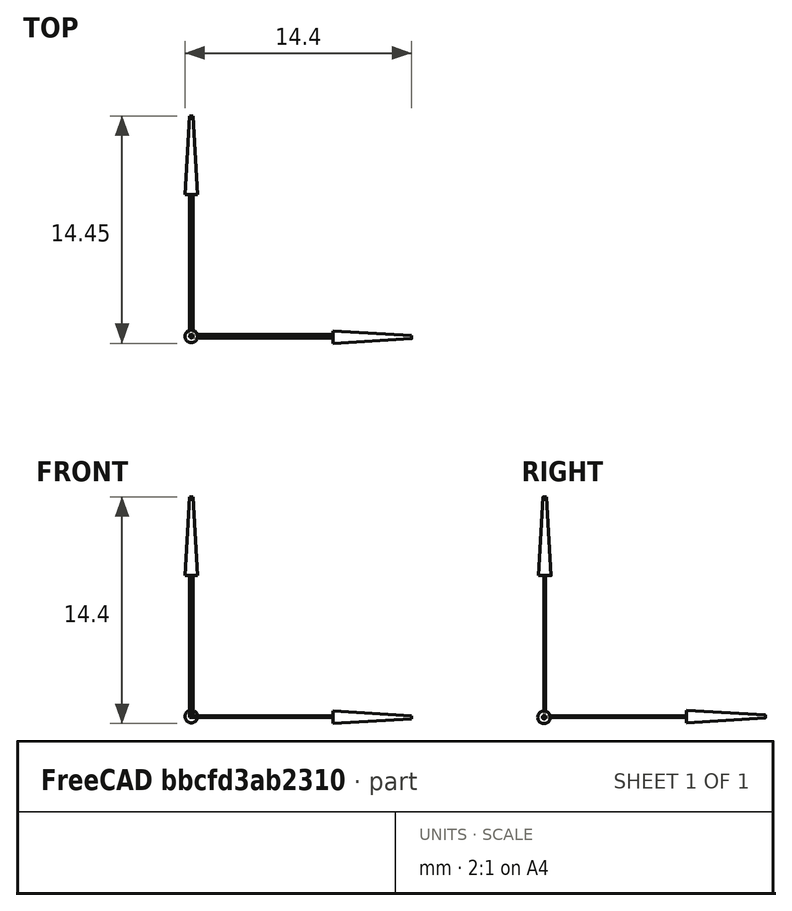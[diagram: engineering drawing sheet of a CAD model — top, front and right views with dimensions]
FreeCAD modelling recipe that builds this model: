
FCSTD DOCUMENT  (FreeCAD 0.16R6458 (Git))
Label: TSM-104-02-X-DH
License: All rights reserved
LicenseURL: http://en.wikipedia.org/wiki/All_rights_reserved
objects: Part::Feature×3, Sketcher::SketchObject×2, App::DocumentObjectGroup×1
note: 5 computed .brp shape members not serialized (recipe doc carries the construction recipe); baked Part::Feature solids carry a one-line shape summary decoded from their .brp

FEATURE [Part::Feature] FusionAxisZ1  label="Z"
  shape: bbox 0.8 x 0.8 x 14 mm, 8 faces (baked)
FEATURE [Part::Feature] FusionAxisY1  label="Y"
  Placement = pos=(0,0,0.05) rot=(-1,0,0;1.5708rad)
  shape: bbox 0.8 x 14 x 0.8 mm, 8 faces (baked)
FEATURE [Part::Feature] FusionAxisX1  label="X"
  Placement = pos=(0,-0.05,0) rot=(0,1,0;1.5708rad)
  shape: bbox 14 x 0.8 x 0.8 mm, 8 faces (baked)
FEATURE [App::DocumentObjectGroup] axis
  Group = -> [FusionAxisZ1,FusionAxisY1,FusionAxisX1]
FEATURE [Sketcher::SketchObject] Sketch001  label="Silcsreen_Helper"
  expr: Constraints[10] = 4 * 2.54mm
  sketch-geometry (4):
    g0: LineSegment StartX=0 StartY=-5.08 StartZ=0 EndX=2.54 EndY=-5.08 EndZ=0
    g1: LineSegment StartX=2.54 StartY=-5.08 StartZ=0 EndX=2.54 EndY=5.08 EndZ=0
    g2: LineSegment StartX=2.54 StartY=5.08 StartZ=0 EndX=0 EndY=5.08 EndZ=0
    g3: LineSegment StartX=0 StartY=5.08 StartZ=0 EndX=0 EndY=-5.08 EndZ=0
  constraints (11):
    c: Coincident(g0,g1)
    c: Coincident(g1,g2)
    c: Coincident(g2,g3)
    c: Coincident(g3,g0)
    c: Horizontal(g0)
    c: Horizontal(g2)
    c: Vertical(g1)
    c: Vertical(g3)
    c: Symmetric(g3,g3,g-1)
    c: DistanceX(g0) = 2.54
    c: DistanceY(g1) = 10.16
FEATURE [Sketcher::SketchObject] Sketch002  label="Footprint_Helper"
  expr: Constraints[133] = 1.19 / 2
  expr: Constraints[129] = (4 - 2) * 2.54mm
  expr: Constraints[10] = 4 * 2.54mm
  sketch-geometry (59):
    g0: LineSegment StartX=0 StartY=-5.08 StartZ=0 EndX=2.54 EndY=-5.08 EndZ=0
    g1: LineSegment StartX=2.54 StartY=-5.08 StartZ=0 EndX=2.54 EndY=5.08 EndZ=0
    g2: LineSegment StartX=2.54 StartY=5.08 StartZ=0 EndX=0 EndY=5.08 EndZ=0
    g3: LineSegment StartX=0 StartY=5.08 StartZ=0 EndX=0 EndY=-5.08 EndZ=0
    g4: LineSegment StartX=4.176 StartY=4.445 StartZ=0 EndX=7.356 EndY=4.445 EndZ=0
    g5: LineSegment StartX=7.356 StartY=4.445 StartZ=0 EndX=7.356 EndY=3.175 EndZ=0
    g6: LineSegment StartX=7.356 StartY=3.175 StartZ=0 EndX=4.176 EndY=3.175 EndZ=0
    g7: LineSegment StartX=4.176 StartY=3.175 StartZ=0 EndX=4.176 EndY=4.445 EndZ=0
    g8: LineSegment StartX=7.986 StartY=4.445 StartZ=0 EndX=11.166 EndY=4.445 EndZ=0
    g9: LineSegment StartX=11.166 StartY=4.445 StartZ=0 EndX=11.166 EndY=3.175 EndZ=0
    g10: LineSegment StartX=11.166 StartY=3.175 StartZ=0 EndX=7.986 EndY=3.175 EndZ=0
    g11: LineSegment StartX=7.986 StartY=3.175 StartZ=0 EndX=7.986 EndY=4.445 EndZ=0
    g12: LineSegment StartX=4.176 StartY=1.905 StartZ=0 EndX=7.356 EndY=1.905 EndZ=0
    g13: LineSegment StartX=7.356 StartY=1.905 StartZ=0 EndX=7.356 EndY=0.635 EndZ=0
    g14: LineSegment StartX=7.356 StartY=0.635 StartZ=0 EndX=4.176 EndY=0.635 EndZ=0
    g15: LineSegment StartX=4.176 StartY=0.635 StartZ=0 EndX=4.176 EndY=1.905 EndZ=0
    g16: LineSegment StartX=7.986 StartY=1.905 StartZ=0 EndX=11.166 EndY=1.905 EndZ=0
    g17: LineSegment StartX=11.166 StartY=1.905 StartZ=0 EndX=11.166 EndY=0.635 EndZ=0
    g18: LineSegment StartX=11.166 StartY=0.635 StartZ=0 EndX=7.986 EndY=0.635 EndZ=0
    g19: LineSegment StartX=7.986 StartY=0.635 StartZ=0 EndX=7.986 EndY=1.905 EndZ=0
    g20: LineSegment StartX=4.176 StartY=-0.635 StartZ=0 EndX=7.356 EndY=-0.635 EndZ=0
    g21: LineSegment StartX=7.356 StartY=-0.635 StartZ=0 EndX=7.356 EndY=-1.905 EndZ=0
    g22: LineSegment StartX=7.356 StartY=-1.905 StartZ=0 EndX=4.176 EndY=-1.905 EndZ=0
    g23: LineSegment StartX=4.176 StartY=-1.905 StartZ=0 EndX=4.176 EndY=-0.635 EndZ=0
    g24: LineSegment StartX=7.986 StartY=-0.635 StartZ=0 EndX=11.166 EndY=-0.635 EndZ=0
    g25: LineSegment StartX=11.166 StartY=-0.635 StartZ=0 EndX=11.166 EndY=-1.905 EndZ=0
    g26: LineSegment StartX=11.166 StartY=-1.905 StartZ=0 EndX=7.986 EndY=-1.905 EndZ=0
    g27: LineSegment StartX=7.986 StartY=-1.905 StartZ=0 EndX=7.986 EndY=-0.635 EndZ=0
    g28: LineSegment StartX=4.176 StartY=-3.175 StartZ=0 EndX=7.356 EndY=-3.175 EndZ=0
    g29: LineSegment StartX=7.356 StartY=-3.175 StartZ=0 EndX=7.356 EndY=-4.445 EndZ=0
    g30: LineSegment StartX=7.356 StartY=-4.445 StartZ=0 EndX=4.176 EndY=-4.445 EndZ=0
    g31: LineSegment StartX=4.176 StartY=-4.445 StartZ=0 EndX=4.176 EndY=-3.175 EndZ=0
    g32: LineSegment StartX=7.986 StartY=-3.175 StartZ=0 EndX=11.166 EndY=-3.175 EndZ=0
    g33: LineSegment StartX=11.166 StartY=-3.175 StartZ=0 EndX=11.166 EndY=-4.445 EndZ=0
    g34: LineSegment StartX=11.166 StartY=-4.445 StartZ=0 EndX=7.986 EndY=-4.445 EndZ=0
    g35: LineSegment StartX=7.986 StartY=-4.445 StartZ=0 EndX=7.986 EndY=-3.175 EndZ=0
    g36: LineSegment [constr] StartX=5.766 StartY=3.81 StartZ=0 EndX=5.766 EndY=1.27 EndZ=0
    g37: LineSegment [constr] StartX=5.766 StartY=1.27 StartZ=0 EndX=5.766 EndY=-1.27 EndZ=0
    g38: LineSegment [constr] StartX=5.766 StartY=-1.27 StartZ=0 EndX=5.766 EndY=-3.81 EndZ=0
    g39: LineSegment [constr] StartX=9.576 StartY=3.81 StartZ=0 EndX=9.576 EndY=1.27 EndZ=0
    g40: LineSegment [constr] StartX=9.576 StartY=1.27 StartZ=0 EndX=9.576 EndY=-1.27 EndZ=0
    g41: LineSegment [constr] StartX=9.576 StartY=-1.27 StartZ=0 EndX=9.576 EndY=-3.81 EndZ=0
    g42: LineSegment [constr] StartX=2.54 StartY=0 StartZ=0 EndX=5.766 EndY=0 EndZ=0
    g43: LineSegment [constr] StartX=5.766 StartY=0 StartZ=0 EndX=9.576 EndY=0 EndZ=0
    g44: LineSegment [constr] StartX=1.27 StartY=-2.54 StartZ=0 EndX=1.27 EndY=2.54 EndZ=0
    g45: LineSegment [constr] StartX=0 StartY=0 StartZ=0 EndX=2.54 EndY=0 EndZ=0
    g46: GeomPoint [constr] X=1.27 Y=0 Z=0
    g47: Circle CenterX=1.27 CenterY=2.54 CenterZ=0 NormalX=0 NormalY=0 NormalZ=1 Radius=0.595
    g48: Circle CenterX=1.27 CenterY=-2.54 CenterZ=0 NormalX=0 NormalY=0 NormalZ=1 Radius=0.595
    g49: LineSegment StartX=2.54 StartY=5.08 StartZ=0 EndX=10.41 EndY=5.08 EndZ=0
    g50: LineSegment StartX=10.41 StartY=5.08 StartZ=0 EndX=10.41 EndY=-5.08 EndZ=0
    g51: LineSegment StartX=10.41 StartY=-5.08 StartZ=0 EndX=2.54 EndY=-5.08 EndZ=0
    g52: LineSegment StartX=0 StartY=5.08 StartZ=0 EndX=-8.13 EndY=5.08 EndZ=0
    g53: LineSegment StartX=-8.13 StartY=5.08 StartZ=0 EndX=-8.13 EndY=-5.08 EndZ=0
    g54: LineSegment StartX=-8.13 StartY=-5.08 StartZ=0 EndX=0 EndY=-5.08 EndZ=0
    g55: LineSegment StartX=-8.4 StartY=5.35 StartZ=0 EndX=11.45 EndY=5.35 EndZ=0
    g56: LineSegment StartX=11.45 StartY=5.35 StartZ=0 EndX=11.45 EndY=-5.35 EndZ=0
    g57: LineSegment StartX=11.45 StartY=-5.35 StartZ=0 EndX=-8.4 EndY=-5.35 EndZ=0
    g58: LineSegment StartX=-8.4 StartY=-5.35 StartZ=0 EndX=-8.4 EndY=5.35 EndZ=0
  constraints (172):
    c: Coincident(g0,g1)
    c: Coincident(g1,g2)
    c: Coincident(g2,g3)
    c: Coincident(g3,g0)
    c: Horizontal(g0)
    c: Horizontal(g2)
    c: Vertical(g1)
    c: Vertical(g3)
    c: Symmetric(g3,g3,g-1)
    c: DistanceX(g0) = 2.54
    c: DistanceY(g1) = 10.16
    c: Coincident(g4,g5)
    c: Coincident(g5,g6)
    c: Coincident(g6,g7)
    c: Coincident(g7,g4)
    c: Horizontal(g4)
    c: Horizontal(g6)
    c: Vertical(g5)
    c: Vertical(g7)
    c: Coincident(g8,g9)
    c: Coincident(g9,g10)
    c: Coincident(g10,g11)
    c: Coincident(g11,g8)
    c: Horizontal(g8)
    c: Horizontal(g10)
    c: Vertical(g9)
    c: Vertical(g11)
    c: Coincident(g12,g13)
    c: Coincident(g13,g14)
    c: Coincident(g14,g15)
    c: Coincident(g15,g12)
    c: Horizontal(g12)
    c: Horizontal(g14)
    c: Vertical(g13)
    c: Vertical(g15)
    c: Coincident(g16,g17)
    c: Coincident(g17,g18)
    c: Coincident(g18,g19)
    c: Coincident(g19,g16)
    c: Horizontal(g16)
    c: Horizontal(g18)
    c: Vertical(g17)
    c: Vertical(g19)
    c: Coincident(g20,g21)
    c: Coincident(g21,g22)
    c: Coincident(g22,g23)
    c: Coincident(g23,g20)
    c: Horizontal(g20)
    c: Horizontal(g22)
    c: Vertical(g21)
    c: Vertical(g23)
    c: Coincident(g24,g25)
    c: Coincident(g25,g26)
    c: Coincident(g26,g27)
    c: Coincident(g27,g24)
    c: Horizontal(g24)
    c: Horizontal(g26)
    c: Vertical(g25)
    c: Vertical(g27)
    c: Coincident(g28,g29)
    c: Coincident(g29,g30)
    c: Coincident(g30,g31)
    c: Coincident(g31,g28)
    c: Horizontal(g28)
    c: Horizontal(g30)
    c: Vertical(g29)
    c: Vertical(g31)
    c: Coincident(g32,g33)
    c: Coincident(g33,g34)
    c: Coincident(g34,g35)
    c: Coincident(g35,g32)
    c: Horizontal(g32)
    c: Horizontal(g34)
    c: Vertical(g33)
    c: Vertical(g35)
    c: Coincident(g36,g37)
    c: Coincident(g37,g38)
    c: Equal(g38,g37)
    c: Equal(g37,g36)
    c: Vertical(g36)
    c: Vertical(g37)
    c: Vertical(g38)
    c: Vertical(g39)
    c: Coincident(g39,g40)
    c: Vertical(g40)
    c: Coincident(g40,g41)
    c: Vertical(g41)
    c: Equal(g41,g40)
    c: Equal(g40,g39)
    c: Equal(g36,g39)
    c: DistanceY(g39) = -2.54
    c: Symmetric(g6,g4,g36)
    c: Symmetric(g12,g14,g36)
    c: Symmetric(g22,g20,g37)
    c: Symmetric(g30,g28,g38)
    c: Symmetric(g10,g8,g39)
    c: Symmetric(g18,g16,g39)
    c: Symmetric(g26,g24,g40)
    c: Symmetric(g32,g34,g41)
    c: Equal(g9,g5)
    c: Equal(g5,g13)
    c: Equal(g13,g21)
    c: Equal(g21,g29)
    c: Equal(g9,g17)
    c: Equal(g17,g25)
    c: Equal(g25,g33)
    c: DistanceY(g9) = -1.27
    c: DistanceX(g8) = 3.18
    c: Equal(g8,g4)
    c: Equal(g4,g12)
    c: Equal(g12,g20)
    c: Equal(g20,g28)
    c: Equal(g8,g16)
    c: Equal(g16,g24)
    c: Equal(g24,g32)
    c: Horizontal(g42)
    c: Coincident(g42,g43)
    c: Horizontal(g43)
    c: Symmetric(g37,g37,g42)
    c: Symmetric(g40,g40,g43)
    c: DistanceX(g43) = 3.81
    c: Vertical(g44)
    c: Horizontal(g45)
    c: Coincident(g45,g42)
    c: Coincident(g45,g-1)
    c: PointOnObject(g42,g1)
    c: Symmetric(g45,g45,g46)
    c: Symmetric(g44,g44,g46)
    c: DistanceX(g46,g42) = 4.496
    c: DistanceY(g44) = 5.08
    c: Coincident(g48,g44)
    c: Coincident(g47,g44)
    c: Equal(g47,g48)
    c: Radius(g47) = 0.595
    c: DistanceX(g-1,g42) = 5.766
    c: DistanceX(g-1,g43) = 9.576
    c: DistanceY(g-1,g41) = -3.81
    c: DistanceY(g-1,g40) = -1.27
    c: Horizontal(g49)
    c: Coincident(g49,g50)
    c: Vertical(g50)
    c: Coincident(g50,g51)
    c: Horizontal(g51)
    c: Coincident(g0,g51)
    c: Coincident(g1,g49)
    c: Coincident(g2,g52)
    c: Horizontal(g52)
    c: Coincident(g52,g53)
    c: Vertical(g53)
    c: Coincident(g53,g54)
    c: Coincident(g54,g0)
    c: Horizontal(g54)
    c: DistanceX(g52) = -8.13
    c: DistanceX(g49) = 7.87
    c: Coincident(g55,g56)
    c: Coincident(g56,g57)
    c: Coincident(g57,g58)
    c: Coincident(g58,g55)
    c: Horizontal(g55)
    c: Horizontal(g57)
    c: Vertical(g56)
    c: Vertical(g58)
    c: DistanceX(g55,g52) = 0.27
    c: DistanceY(g52,g55) = 0.27
    c: DistanceY(g56,g50) = 0.27
    c: DistanceX(g33,g56) = 0.284
    c: DistanceX(g57) = -8.4
    c: DistanceY(g57) = -5.35
    c: DistanceX(g55) = 11.45
    c: DistanceY(g55) = 5.35
    c: DistanceX(g-1,g49) = 10.41
    c: DistanceY(g-1,g2) = 5.08
